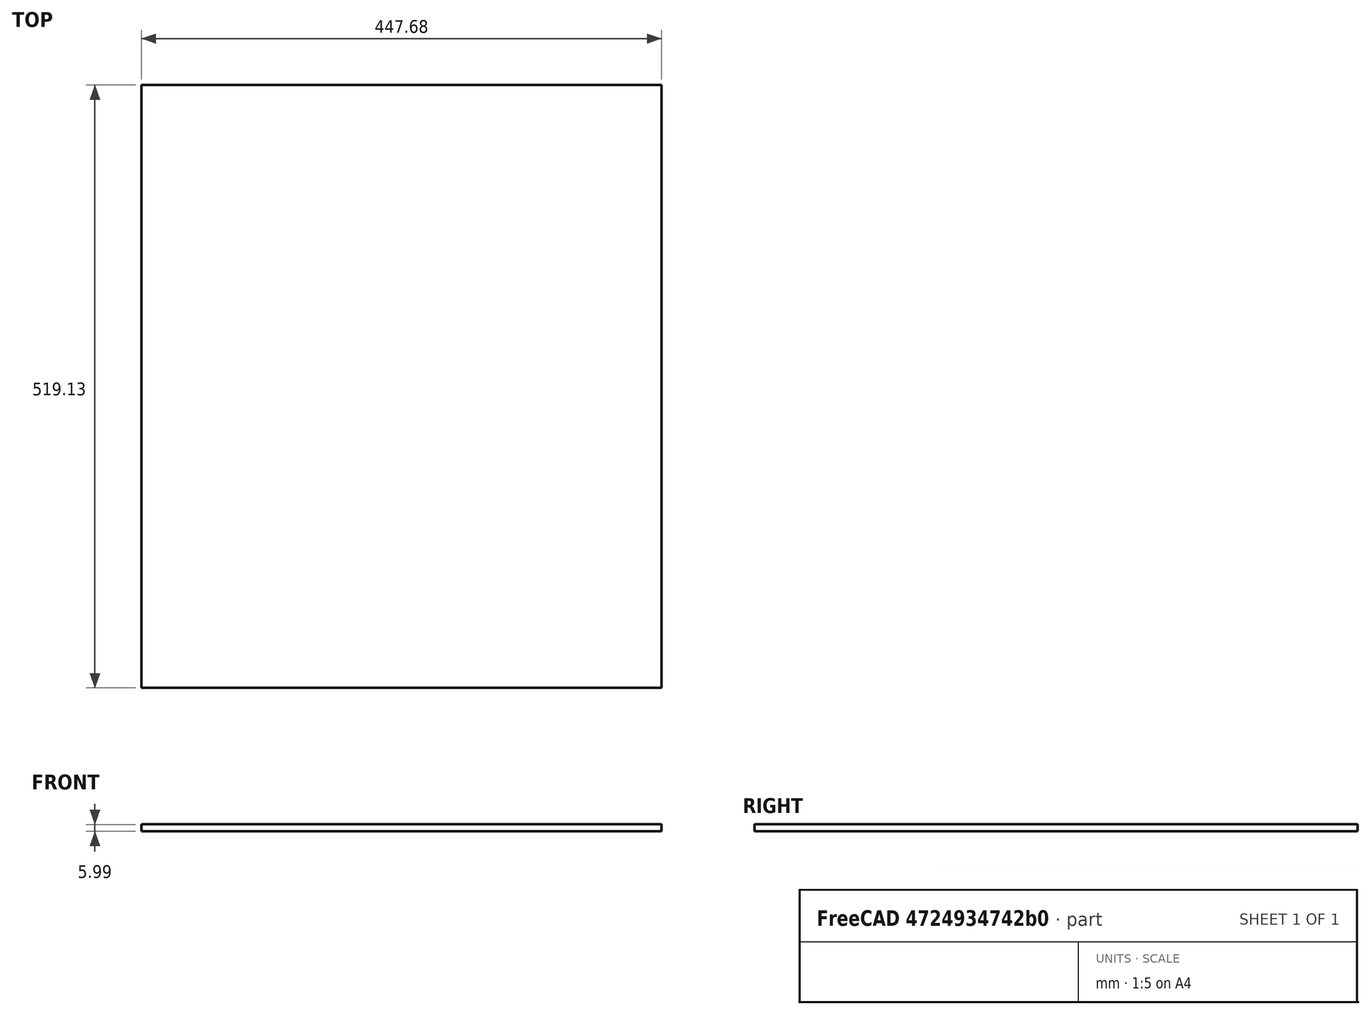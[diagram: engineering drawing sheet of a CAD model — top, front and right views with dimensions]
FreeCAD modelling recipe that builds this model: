
FCSTD DOCUMENT  (FreeCAD 0.19R24267 (Git))
Label: Up1-P8
License: All rights reserved
LicenseURL: http://en.wikipedia.org/wiki/All_rights_reserved
objects: TechDraw::DrawViewDimension×3, TechDraw::DrawProjGroupItem×2, TechDraw::DrawHatch×2, TechDraw::DrawViewAnnotation×2, Sketcher::SketchObject×1, Part::Extrusion×1, TechDraw::DrawSVGTemplate×1, TechDraw::DrawProjGroup×1, TechDraw::DrawPage×1
note: 2 computed .brp shape members not serialized (recipe doc carries the construction recipe); baked Part::Feature solids carry a one-line shape summary decoded from their .brp

FEATURE [Sketcher::SketchObject] Sketch
  FullyConstrained = false
  sketch-geometry (4):
    g0: LineSegment StartX=0 StartY=0 StartZ=0 EndX=447.675 EndY=0 EndZ=0
    g1: LineSegment StartX=447.675 StartY=0 StartZ=0 EndX=447.675 EndY=519.125 EndZ=0
    g2: LineSegment StartX=447.675 StartY=519.125 StartZ=0 EndX=0 EndY=519.125 EndZ=0
    g3: LineSegment StartX=0 StartY=519.125 StartZ=0 EndX=0 EndY=0 EndZ=0
  constraints (11):
    c: Coincident(g0,g1)
    c: Coincident(g1,g2)
    c: Coincident(g2,g3)
    c: Coincident(g3,g0)
    c: Horizontal(g0)
    c: Horizontal(g2)
    c: Vertical(g1)
    c: Vertical(g3)
    c: Coincident(g0,g-1)
    c: DistanceX(g2,g2) = 447.675
    c: DistanceY(g3,g3) = 519.125
FEATURE [Part::Extrusion] Extrude
  Base = -> Sketch
  Dir = (0,0,1)
  DirMode = 2
  FaceMakerClass = Part::FaceMakerBullseye
  LengthFwd = 5.9944
  LengthRev = 0
  Solid = true
  Symmetric = false
FEATURE [TechDraw::DrawSVGTemplate] Template
  Height = 215.9
  Orientation = 1
  Width = 279.4
FEATURE [TechDraw::DrawProjGroupItem] ProjItem  label="Front"
  CoarseView = false
  Direction = (0,0,1)
  Focus = 100
  HardHidden = false
  IsoCount = 0
  IsoHidden = false
  IsoVisible = false
  LockPosition = true
  Perspective = false
  Rotation = 0
  RotationVector = (1,0,0)
  Scale = 0.25
  ScaleType = 2
  SeamHidden = false
  SeamVisible = true
  SmoothHidden = false
  SmoothVisible = true
  Source = -> [Extrude]
  Type = 0
  X = 0
  XDirection = (1,0,0)
  Y = 0
FEATURE [TechDraw::DrawProjGroupItem] ProjItem001  label="Left"
  CoarseView = false
  Direction = (-1,0,1e-16)
  Focus = 100
  HardHidden = false
  IsoCount = 0
  IsoHidden = false
  IsoVisible = false
  LockPosition = false
  Perspective = false
  Rotation = 0
  RotationVector = (1,0,0)
  Scale = 0.25
  ScaleType = 2
  SeamHidden = false
  SeamVisible = true
  SmoothHidden = false
  SmoothVisible = true
  Source = -> [Extrude]
  Type = 1
  X = 84.5403
  XDirection = (1e-16,0,1)
  Y = 0
FEATURE [TechDraw::DrawProjGroup] ProjGroup
  Anchor = -> ProjItem
  AutoDistribute = true
  LockPosition = false
  ProjectionType = 0
  Rotation = 0
  Scale = 0.25
  ScaleType = 2
  Source = -> [Extrude]
  Views = -> [ProjItem,ProjItem001]
  X = 139.7
  Y = 107.95
  spacingX = 15.0114
  spacingY = 15.0114
FEATURE [TechDraw::DrawViewDimension] Dimension
  Arbitrary = false
  ArbitraryTolerances = false
  EqualTolerance = true
  FormatSpec = %.3f
  FormatSpecOverTolerance = %+.3f
  FormatSpecUnderTolerance = %+.3f
  Inverted = false
  LockPosition = false
  MeasureType = 1
  OverTolerance = 0
  References2D = -> [ProjItem]
  Rotation = 0
  ScaleType = 0
  TheoreticalExact = false
  Type = 1
  UnderTolerance = 0
  X = 0
  Y = -74.1593
FEATURE [TechDraw::DrawViewDimension] Dimension001
  Arbitrary = false
  ArbitraryTolerances = false
  EqualTolerance = true
  FormatSpec = %.3f
  FormatSpecOverTolerance = %+.3f
  FormatSpecUnderTolerance = %+.3f
  Inverted = false
  LockPosition = false
  MeasureType = 1
  OverTolerance = 0
  References2D = -> [ProjItem]
  Rotation = 0
  ScaleType = 0
  TheoreticalExact = false
  Type = 2
  UnderTolerance = 0
  X = 62.6177
  Y = 0.105607
FEATURE [TechDraw::DrawHatch] Hatch  label="HatchF0"
  HatchPattern = <path>
  Source = -> ProjItem [Face0]
FEATURE [TechDraw::DrawHatch] Hatch001  label="Hatch001F0"
  HatchPattern = <path>
  Source = -> ProjItem001 [Face0]
FEATURE [TechDraw::DrawViewDimension] Dimension002
  Arbitrary = false
  ArbitraryTolerances = false
  EqualTolerance = true
  FormatSpec = %.3f
  FormatSpecOverTolerance = %+.3f
  FormatSpecUnderTolerance = %+.3f
  Inverted = false
  LockPosition = false
  MeasureType = 1
  OverTolerance = 0
  References2D = -> [ProjItem001]
  Rotation = 0
  ScaleType = 0
  TheoreticalExact = false
  Type = 1
  UnderTolerance = 0
  X = 21.3506
  Y = 54.0101
FEATURE [TechDraw::DrawViewAnnotation] Annotation
  Font = osifont
  LineSpace = 80
  LockPosition = false
  MaxWidth = -1
  Rotation = 0
  ScaleType = 0
  Text = Figure S3 (Upright) | Panel 8 [front left] | Quantity: 1
  TextSize = 5.0038
  TextStyle = 0
  X = 30.165
  Y = 195.58
FEATURE [TechDraw::DrawViewAnnotation] Annotation002
  Font = osifont
  LineSpace = 80
  LockPosition = false
  MaxWidth = -1
  Rotation = 0
  ScaleType = 0
  Text = Units: Inches
  TextSize = 5.0038
  TextStyle = 0
  X = 259.08
  Y = 5.08
FEATURE [TechDraw::DrawPage] Page
  KeepUpdated = true
  NextBalloonIndex = 1
  ProjectionType = 0
  Template = -> Template
  Views = -> [ProjGroup,Dimension,Dimension001,Dimension002,Annotation,Annotation002]
note: 2 file-system paths scrubbed to <path> (originals preserved in the JSON sidecar)
